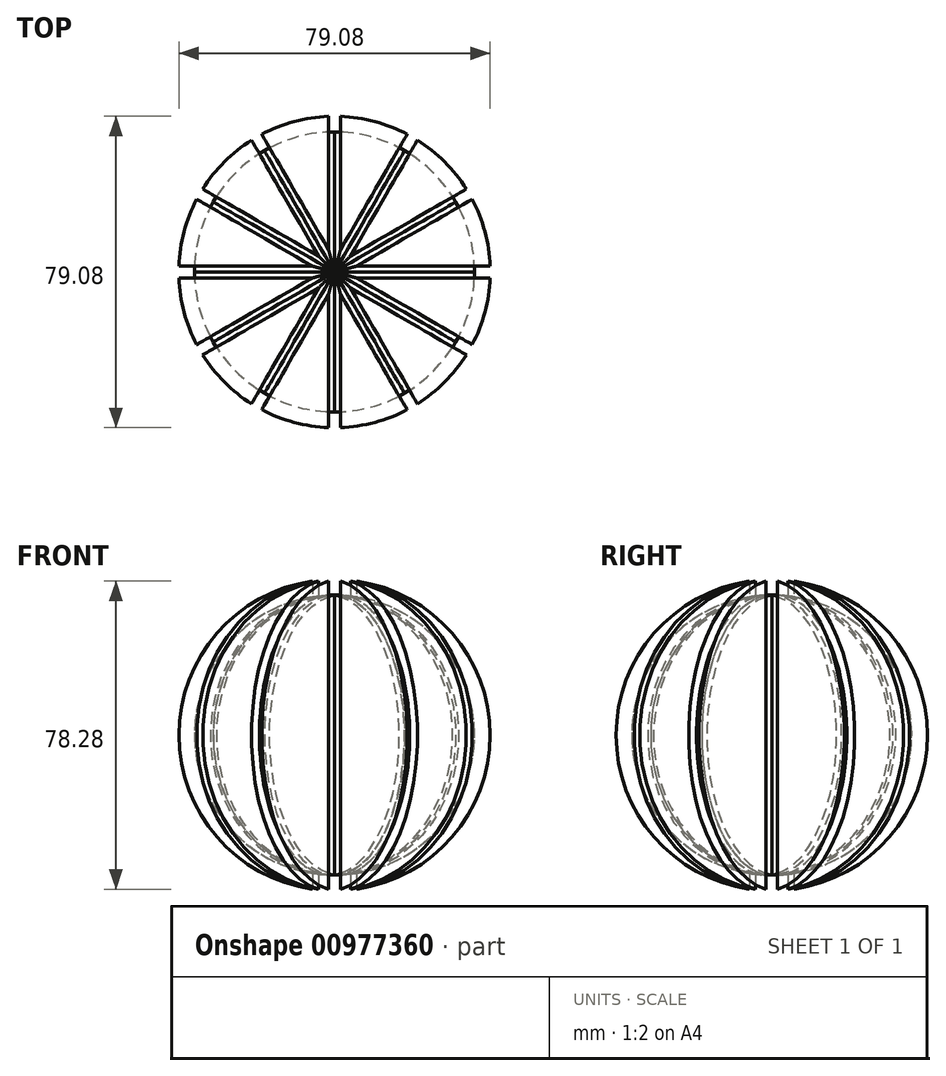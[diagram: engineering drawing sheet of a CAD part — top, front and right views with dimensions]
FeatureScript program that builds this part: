
annotation { "Feature Type Name" : "Feature", "Feature Type Description" : "" }
export const myFeature = defineFeature(function(context is Context, id is Id, definition is map)
    precondition{}
    {
        {
            var Q0;
            Q0=qCreatedBy(makeId("Front.planeOp"),FACE);
            var sketch = newSketch(context, id + "F0", { "sketchPlane" : qUnion([Q0])});
            skCircle(sketch, "E0", {"center": v(0, 0) * mm, "radius": 39.57 * mm});
            skCircle(sketch, "E1", {"center": v(0, 0) * mm, "radius": 35.56 * mm});
            skLineSegment(sketch, "E2", {"start": v(0, 42.74) * mm, "end": v(0, -46.26) * mm});
            skSolve(sketch);
        }
        {
            var Q0;
            {var subQ0=sQuery(id+"F0.wireOp",EDGE,"E2");var subQ1=sQuery(id+"F0.wireOp",EDGE,"E0");var subQ2=makeQuery(id+"F0.imprint","INTERSECT",VERTEX,{"disambiguationData":[OD(0.0)],"derivedFrom":[subQ1,subQ0]});Q0=makeQuery(id+"F0.imprint","IMPRINT",FACE,{"disambiguationData":[TD([[makeQuery(id+"F0.imprint","IMPRINT",EDGE,{"disambiguationData":[TD([[subQ2,-1.0]])],"derivedFrom":subQ1}),1.0]])]});}
            var Q1;
            Q1=sQuery(id+"F0.wireOp",EDGE,"E2");
            revolve(context, id + "F1", {"surfaceOperationType" : NewSurfaceOperationType.NEW, "entities" : qUnion([Q0]), "axis" : qUnion([Q1]), "revolveType" : RevolveType.FULL});
        }
        {
            var Q0;
            Q0=qCreatedBy(makeId("Top.planeOp"),FACE);
            var sketch = newSketch(context, id + "F2", { "sketchPlane" : qUnion([Q0])});
            skLineSegment(sketch, "E3", {"start": v(-26.92, 29.04) * mm, "end": v(-29.04, 26.92) * mm});
            skLineSegment(sketch, "E4", {"start": v(-29.04, 26.92) * mm, "end": v(-26.2, 24.09) * mm});
            skLineSegment(sketch, "E5", {"start": v(-26.2, 24.09) * mm, "end": v(-24.09, 26.2) * mm});
            skLineSegment(sketch, "E6", {"start": v(-24.09, 26.2) * mm, "end": v(-26.92, 29.04) * mm});
            skLineSegment(sketch, "E7", {"start": v(-1.5, 39.57) * mm, "end": v(-1.5, 35.56) * mm});
            skLineSegment(sketch, "E8", {"start": v(-1.5, 35.56) * mm, "end": v(1.5, 35.56) * mm});
            skLineSegment(sketch, "E9", {"start": v(1.5, 35.56) * mm, "end": v(1.5, 39.57) * mm});
            skLineSegment(sketch, "E10", {"start": v(-1.5, 39.57) * mm, "end": v(1.5, 39.57) * mm});
            skLineSegment(sketch, "E11", {"start": v(26.2, 24.09) * mm, "end": v(29.04, 26.92) * mm});
            skLineSegment(sketch, "E12", {"start": v(29.04, 26.92) * mm, "end": v(26.92, 29.04) * mm});
            skLineSegment(sketch, "E13", {"start": v(26.92, 29.04) * mm, "end": v(24.09, 26.2) * mm});
            skLineSegment(sketch, "E14", {"start": v(24.09, 26.2) * mm, "end": v(26.2, 24.09) * mm});
            skLineSegment(sketch, "E15", {"start": v(35.56, -1.5) * mm, "end": v(39.57, -1.5) * mm});
            skLineSegment(sketch, "E16", {"start": v(39.57, -1.5) * mm, "end": v(39.57, 1.5) * mm});
            skLineSegment(sketch, "E17", {"start": v(39.57, 1.5) * mm, "end": v(35.56, 1.5) * mm});
            skLineSegment(sketch, "E18", {"start": v(35.56, 1.5) * mm, "end": v(35.56, -1.5) * mm});
            skLineSegment(sketch, "E19", {"start": v(0, 0) * mm, "end": v(20.78, -20.78) * mm});
            skLineSegment(sketch, "E20", {"start": v(0, 0) * mm, "end": v(-18.1, -18.1) * mm});
            skLineSegment(sketch, "E21", {"start": v(0, 0) * mm, "end": v(-26.14, 0) * mm});
            skLineSegment(sketch, "E22", {"start": v(0, 0) * mm, "end": v(0, -24.92) * mm});
            skLineSegment(sketch, "E23", {"start": v(0, 0) * mm, "end": v(32.57, 32.57) * mm, "construction": true});
            skLineSegment(sketch, "E24", {"start": v(0, 0) * mm, "end": v(-36.94, 36.94) * mm, "construction": true});
            skSolve(sketch);
        }
        {
            var Q0;
            Q0=makeQuery(id+"F2.imprint","IMPRINT",FACE,{"disambiguationData":[TD([[makeQuery(id+"F2.imprint","IMPRINT",EDGE,{"derivedFrom":sQuery(id+"F2.wireOp",EDGE,"E15")}),1.0]])]});
            var Q1;
            Q1=sQuery(id+"F2.wireOp",EDGE,"E22");
            revolve(context, id + "F3", {"surfaceOperationType" : NewSurfaceOperationType.NEW, "entities" : qUnion([Q0]), "axis" : qUnion([Q1]), "revolveType" : RevolveType.FULL, "oppositeDirection" : true});
        }
        {
            var Q0;
            Q0=qCreatedBy(makeId("Right.planeOp"),FACE);
            var sketch = newSketch(context, id + "F4", { "sketchPlane" : qUnion([Q0])});
            skLineSegment(sketch, "E25", {"start": v(0, -53.87) * mm, "end": v(0, 65.26) * mm});
            skSolve(sketch);
        }
        {
            var Q0;
            Q0=makeQuery(id+"F3.opRevolve","SWEPT_BODY",BODY,{"disambiguationData":[OSD([sQuery(id+"F2.wireOp",EDGE,"E15"),sQuery(id+"F2.wireOp",EDGE,"E16"),sQuery(id+"F2.wireOp",EDGE,"E17"),sQuery(id+"F2.wireOp",EDGE,"E18")])]});
            var Q1;
            Q1=sQuery(id+"F4.wireOp",EDGE,"E25");
            circularPattern(context, id + "F5", {"operationType" : NewBodyOperationType.REMOVE, "entities" : qUnion([Q0]), "axis" : qUnion([Q1]), "angle" : 360 * degree, "instanceCount" : 12, "equalSpace" : true});
        }
    });
